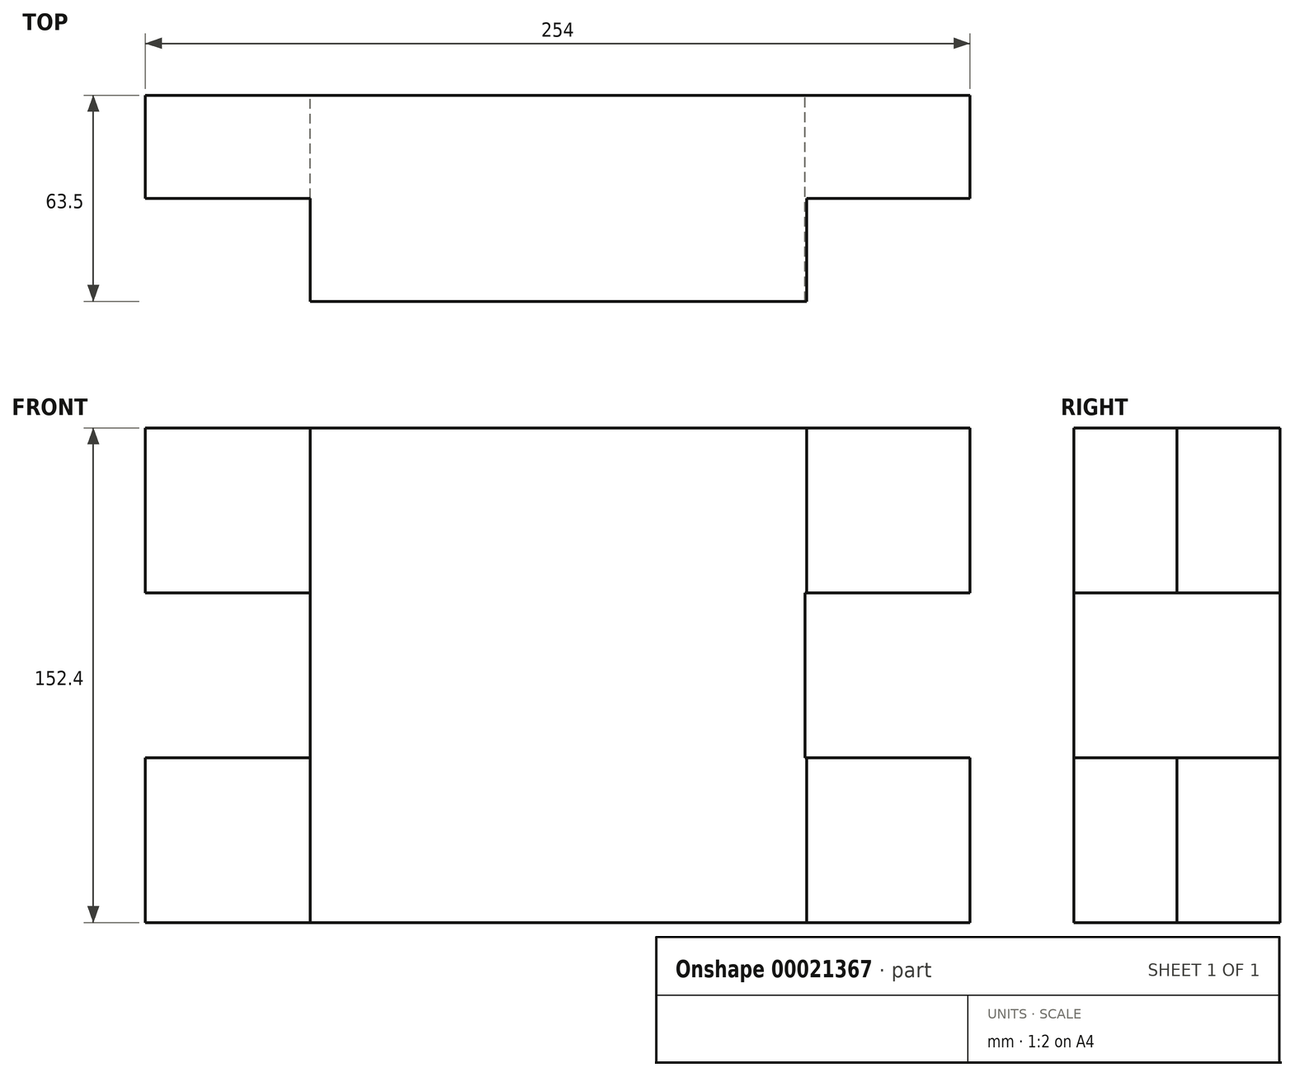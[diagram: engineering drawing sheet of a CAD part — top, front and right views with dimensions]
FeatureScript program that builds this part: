
annotation { "Feature Type Name" : "Feature", "Feature Type Description" : "" }
export const myFeature = defineFeature(function(context is Context, id is Id, definition is map)
    precondition{}
    {
        {
            var Q0;
            Q0=qCreatedBy(makeId("Front.planeOp"),FACE);
            var sketch = newSketch(context, id + "F0", { "sketchPlane" : qUnion([Q0])});
            skLineSegment(sketch, "E0.bottom", {"start": v(-105.38, 97.89) * mm, "end": v(148.62, 97.89) * mm});
            skLineSegment(sketch, "E0.top", {"start": v(-105.38, -54.51) * mm, "end": v(148.62, -54.51) * mm});
            skLineSegment(sketch, "E0.left", {"start": v(-105.38, 97.89) * mm, "end": v(-105.38, 47.09) * mm});
            skLineSegment(sketch, "E0.right", {"start": v(148.62, 97.89) * mm, "end": v(148.62, 47.09) * mm});
            skLineSegment(sketch, "E1.bottom", {"start": v(-105.38, 47.09) * mm, "end": v(-54.58, 47.09) * mm});
            skLineSegment(sketch, "E1.top", {"start": v(-105.38, -3.71) * mm, "end": v(-54.58, -3.71) * mm});
            skLineSegment(sketch, "E1.right", {"start": v(-54.58, 47.09) * mm, "end": v(-54.58, -3.71) * mm});
            skLineSegment(sketch, "E2.trimOffspring", {"start": v(-105.38, -3.71) * mm, "end": v(-105.38, -54.51) * mm});
            skLineSegment(sketch, "E3.bottom", {"start": v(148.62, 47.09) * mm, "end": v(97.82, 47.09) * mm});
            skLineSegment(sketch, "E3.top", {"start": v(148.62, -3.71) * mm, "end": v(97.82, -3.71) * mm});
            skLineSegment(sketch, "E3.right", {"start": v(97.82, 47.09) * mm, "end": v(97.82, -3.71) * mm});
            skLineSegment(sketch, "E4.trimOffspring", {"start": v(148.62, -3.71) * mm, "end": v(148.62, -54.51) * mm});
            skSolve(sketch);
        }
        {
            var Q0;
            Q0=makeQuery(id+"F0.imprint","IMPRINT",FACE,{"disambiguationData":[TD([[makeQuery(id+"F0.imprint","IMPRINT",EDGE,{"derivedFrom":sQuery(id+"F0.wireOp",EDGE,"E0.bottom")}),-1.0]])]});
            var sketch = newSketch(context, id + "F1", { "sketchPlane" : qUnion([Q0])});
            skSolve(sketch);
        }
        {
            var Q0;
            Q0=makeQuery(id+"F1.imprint","IMPRINT",FACE,{"disambiguationData":[TD([[makeQuery(id+"F1.imprint","IMPRINT",EDGE,{"derivedFrom":makeQuery(id+"F0.imprint","IMPRINT",EDGE,{"derivedFrom":sQuery(id+"F0.wireOp",EDGE,"E0.bottom")})}),-1.0]])]});
            extrude(context, id + "F2", {"entities" : qUnion([Q0]), "depth" : 31.75 * mm});
        }
        {
            var Q0;
            Q0=makeQuery(id+"F2.opExtrude","CAP_FACE",FACE,{"disambiguationData":[OSD([sQuery(id+"F0.wireOp",EDGE,"E0.bottom"),sQuery(id+"F0.wireOp",EDGE,"E0.top"),sQuery(id+"F0.wireOp",EDGE,"E0.left"),sQuery(id+"F0.wireOp",EDGE,"E1.bottom"),sQuery(id+"F0.wireOp",EDGE,"E1.top"),sQuery(id+"F0.wireOp",EDGE,"E1.right"),sQuery(id+"F0.wireOp",EDGE,"E2.trimOffspring"),sQuery(id+"F0.wireOp",EDGE,"E0.right"),sQuery(id+"F0.wireOp",EDGE,"E3.bottom"),sQuery(id+"F0.wireOp",EDGE,"E3.top"),sQuery(id+"F0.wireOp",EDGE,"E3.right"),sQuery(id+"F0.wireOp",EDGE,"E4.trimOffspring")])],"isStart":false});
            var sketch = newSketch(context, id + "F3", { "sketchPlane" : qUnion([Q0])});
            skLineSegment(sketch, "E5.bottom", {"start": v(-54.58, 97.89) * mm, "end": v(98.27, 97.89) * mm});
            skLineSegment(sketch, "E5.top", {"start": v(-54.58, -54.51) * mm, "end": v(98.27, -54.51) * mm});
            skLineSegment(sketch, "E5.left", {"start": v(-54.58, 97.89) * mm, "end": v(-54.58, -54.51) * mm});
            skLineSegment(sketch, "E5.right", {"start": v(98.27, 97.89) * mm, "end": v(98.27, -54.51) * mm});
            skSolve(sketch);
        }
        {
            var Q0;
            {var subQ9=sQuery(id+"F3.wireOp",EDGE,"E5.bottom");Q0=makeQuery(id+"F3.imprint","IMPRINT",FACE,{"disambiguationData":[TD([[makeQuery(id+"F3.imprint","IMPRINT",EDGE,{"derivedFrom":subQ9}),-1.0]])]});}
            extrude(context, id + "F4", {"entities" : qUnion([Q0]), "operationType" : NewBodyOperationType.ADD, "depth" : 31.75 * mm});
        }
    });
